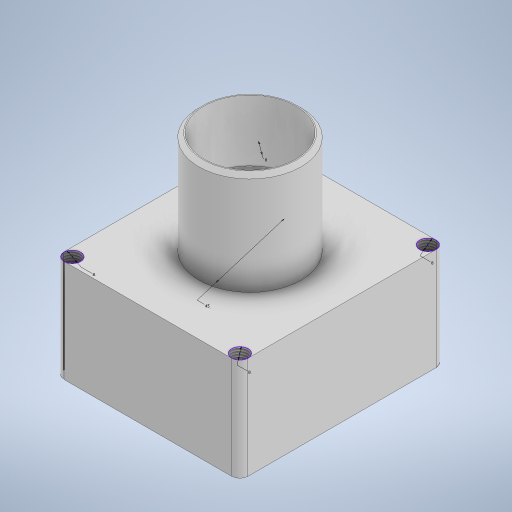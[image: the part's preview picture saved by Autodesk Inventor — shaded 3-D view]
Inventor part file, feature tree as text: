
AUTODESK INVENTOR PART (.ipt)
format: ipt  version: 2024 (Build 280153000, 153)  size: 324,608 bytes
history: native  units: mm
features: hole x4, thread x4, extrude x3, sketch x3, fillet x2, chamfer x1
ambient origin geometry x8: Origin, YZ Plane, XZ Plane, XY Plane, X Axis, Y Axis, Z Axis, Center Point
bodies: Solid1 (feature_tree)
feature tree (17):
  extrude  "Extrusion1"  Depth=100.0mm
  extrude  "Extrusion2"  Depth=50.0mm
  fillet  "Fillet1"  Radius=50.0mm
  fillet  "Fillet2"  Radius=4.0mm
  sketch  "Sketch4"  dims[d3=50.0mm d4=0.0mm d5=50.0mm d6=50.0mm d7=0.0mm d8=4.0mm]
  extrude  "Extrusion3"  Depth=50.0mm
  hole  "Hole1"  [1 undecoded]
  hole  "Hole2"  [1 undecoded]
  hole  "Hole3"  [1 undecoded]
  hole  "Hole4"  [1 undecoded]
  thread  "Thread1"  [1 undecoded]
  thread  "Thread2"  [1 undecoded]
  thread  "Thread3"  [1 undecoded]
  thread  "Thread4"  [1 undecoded]
  chamfer  "Chamfer1"  Distance=50.0mm
  sketch  "Sketch9"  dims[d9=4.0mm d16=45.0mm d17=45.0mm d18=30.0mm d19=0.0mm d20=8.0mm d21=8.0mm d22=8.0mm d23=8.0mm d24=8.0mm d25=6.0mm d26=4.0mm d27=2.0mm d28=90.0deg d29=8.0mm d30=20.594885mm d31=8.0mm d32=6.0mm d33=4.0mm d34=2.0mm d35=90.0deg d36=8.0mm d37=20.594885mm d38=8.0mm d39=6.0mm d40=4.0mm d41=2.0mm d42=90.0deg d43=8.0mm d44=20.594885mm d45=8.0mm d46=6.0mm d47=4.0mm d48=2.0mm d49=90.0deg d50=8.0mm d51=20.594885mm d52=50.0mm d53=0.0mm d54=50.0mm d55=0.0mm d56=50.0mm d57=0.0mm d58=50.0mm d59=0.0mm d60=2.0mm d61=2.0mm d62=45.0deg d63=0.375mm]
  sketch  "Sketch1"  dims[d0=90.0mm d1=100.0mm]
note: 8 required parameter values undecoded (feature->parameter linkage not recoverable at this tier; creation-order binding heuristic only, values carry confidence <= 0.55)
